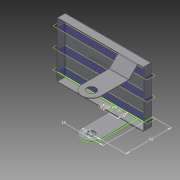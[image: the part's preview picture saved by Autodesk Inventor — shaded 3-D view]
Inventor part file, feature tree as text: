
AUTODESK INVENTOR PART (.ipt)
format: ipt  version: 2013 (Build 170138000, 138)  size: 250,880 bytes
history: native  units: mm
features: sheet_metal_op x10, sketch x7, other x4, plane x3, hole x2, extrude x1
ambient origin geometry x8: Origin, YZ Plane, XZ Plane, XY Plane, X Axis, Y Axis, Z Axis, Center Point
bodies: Solid1 (feature_tree)
feature tree (27):
  sheet_metal_op  "Face1"
  sheet_metal_op  "Flange1"
  sketch  "Sketch3"  dims[d17=1.0mm d18=0.5mm]
  plane  "Work Plane1"
  sketch  "Sketch4"  dims[d19=8.0mm d20=90.0deg d21=0.5mm]
  plane  "Work Plane2"
  sketch  "Sketch5"  dims[d22=2.0mm]
  plane  "Work Plane3"
  sketch  "Sketch6"  dims[d23=0.5mm]
  sheet_metal_op  "Face3"
  sheet_metal_op  "Face4"
  sheet_metal_op  "Bend5"
  sheet_metal_op  "Bend6"
  hole  "Hole1"  [1 undecoded]
  hole  "Hole2"  [1 undecoded]
  extrude  "Extrusion1"  Depth=0.5mm
  sketch  "Sketch1"  dims[d0=83.0mm d1=53.0mm d2=70.0mm d3=40.0mm d4=13.0mm d6=13.0mm d7=13.0mm d8=7.0mm d9=4.0mm d10=4.0mm d11=4.0mm d12=4.0mm d13=3.0mm d14=0.5mm]
  other  "Plate1"
  sketch  "Sketch2"  dims[d15=0.5mm d16=0.25mm]
  other  "Plate2"
  sheet_metal_op  "Bend1"
  sheet_metal_op  "Corner1"
  other  "Plate4"
  sheet_metal_op  "Bend3"
  other  "Plate5"
  sheet_metal_op  "Bend4"
  sketch  "Sketch7"  dims[d24=0.5mm d25=43.0mm d26=15.0mm d27=18.3mm d28=10.0mm d29=10.0mm d30=90.0deg d36=-26.5mm d37=43.0mm d38=15.0mm d39=18.3mm d40=10.0mm d41=10.0mm d42=90.0deg d43=18.0mm d44=43.0mm d45=15.0mm d46=18.3mm d47=10.0mm d48=10.0mm d49=90.0deg d50=-18.0mm d51=43.0mm d52=15.0mm d53=18.3mm d54=10.0mm d55=10.0mm d56=90.0deg d57=0.5mm d58=0.5mm d59=0.25mm d60=1.0mm d61=0.5mm d62=0.5mm d63=0.5mm d64=0.25mm d65=1.0mm d66=0.5mm d67=0.5mm d68=0.25mm d69=1.0mm d70=0.5mm d71=0.5mm d72=0.5mm d73=0.25mm d74=1.0mm d75=0.5mm d76=0.5mm d77=8.5mm d78=6.0mm d79=4.0mm d80=2.0mm d81=90.0deg d82=0.5mm d83=20.594885mm d84=6.6mm d85=6.0mm d86=12.6mm d87=2.0mm d88=90.0deg d89=0.5mm d90=20.594885mm d91=32.0mm d92=83.0mm d93=53.0mm d94=70.0mm d95=40.0mm d96=13.0mm d97=13.0mm d98=32.0mm d99=7.0mm d100=4.0mm d101=4.0mm d102=4.0mm d103=4.0mm d104=3.0mm d105=13.0mm d106=1.0mm d107=0.0mm]
note: 2 required parameter values undecoded (feature->parameter linkage not recoverable at this tier; creation-order binding heuristic only, values carry confidence <= 0.55)
